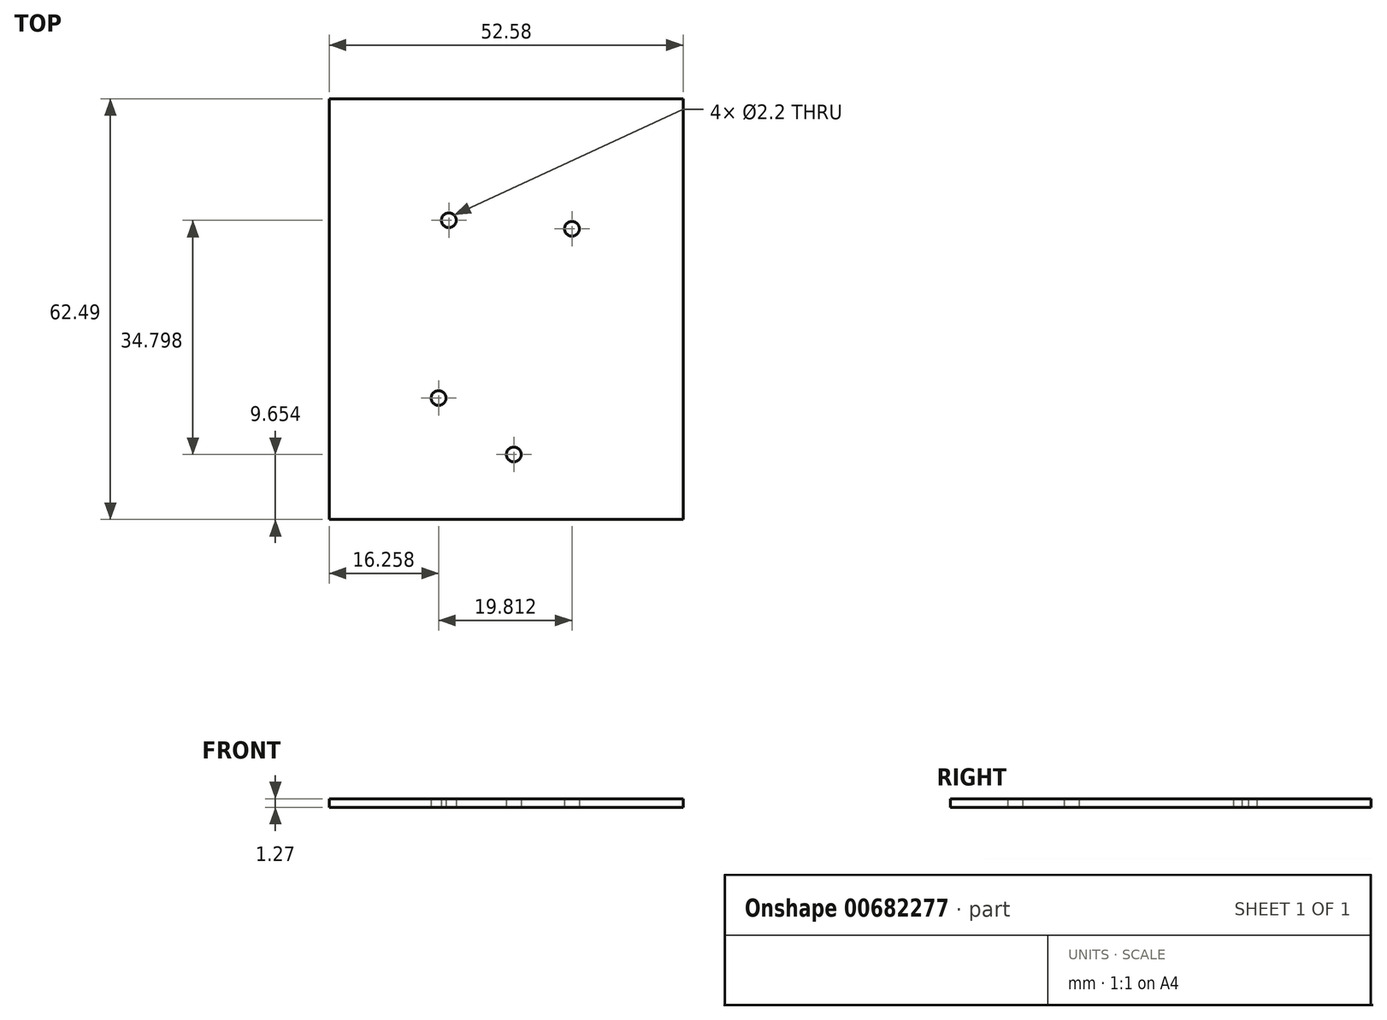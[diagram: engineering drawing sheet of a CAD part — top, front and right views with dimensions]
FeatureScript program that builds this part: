
annotation { "Feature Type Name" : "Feature", "Feature Type Description" : "" }
export const myFeature = defineFeature(function(context is Context, id is Id, definition is map)
    precondition{}
    {
        {
            var Q0;
            Q0=qCreatedBy(makeId("Top.planeOp"),FACE);
            var sketch = newSketch(context, id + "F0", { "sketchPlane" : qUnion([Q0])});
            skLineSegment(sketch, "E0.bottom", {"start": v(4.57, 82.3) * mm, "end": v(57.15, 82.3) * mm});
            skLineSegment(sketch, "E0.top", {"start": v(4.57, 19.81) * mm, "end": v(57.15, 19.81) * mm});
            skLineSegment(sketch, "E0.left", {"start": v(57.15, 19.81) * mm, "end": v(57.15, 82.3) * mm});
            skLineSegment(sketch, "E0.right", {"start": v(4.57, 19.81) * mm, "end": v(4.57, 82.3) * mm});
            skCircle(sketch, "E1", {"center": v(22.35, 64.26) * mm, "radius": 1.1 * mm});
            skCircle(sketch, "E2", {"center": v(40.64, 63) * mm, "radius": 1.1 * mm});
            skCircle(sketch, "E3", {"center": v(20.83, 37.85) * mm, "radius": 1.1 * mm});
            skCircle(sketch, "E4", {"center": v(32, 29.46) * mm, "radius": 1.1 * mm});
            skSolve(sketch);
        }
        {
            var Q0;
            Q0 = qSketchRegion(id + "F0", true);
            extrude(context, id + "F1", {"entities" : qUnion([Q0]), "depth" : 1.27 * mm, "offsetDistance" : 25.4 * mm});
        }
    });
